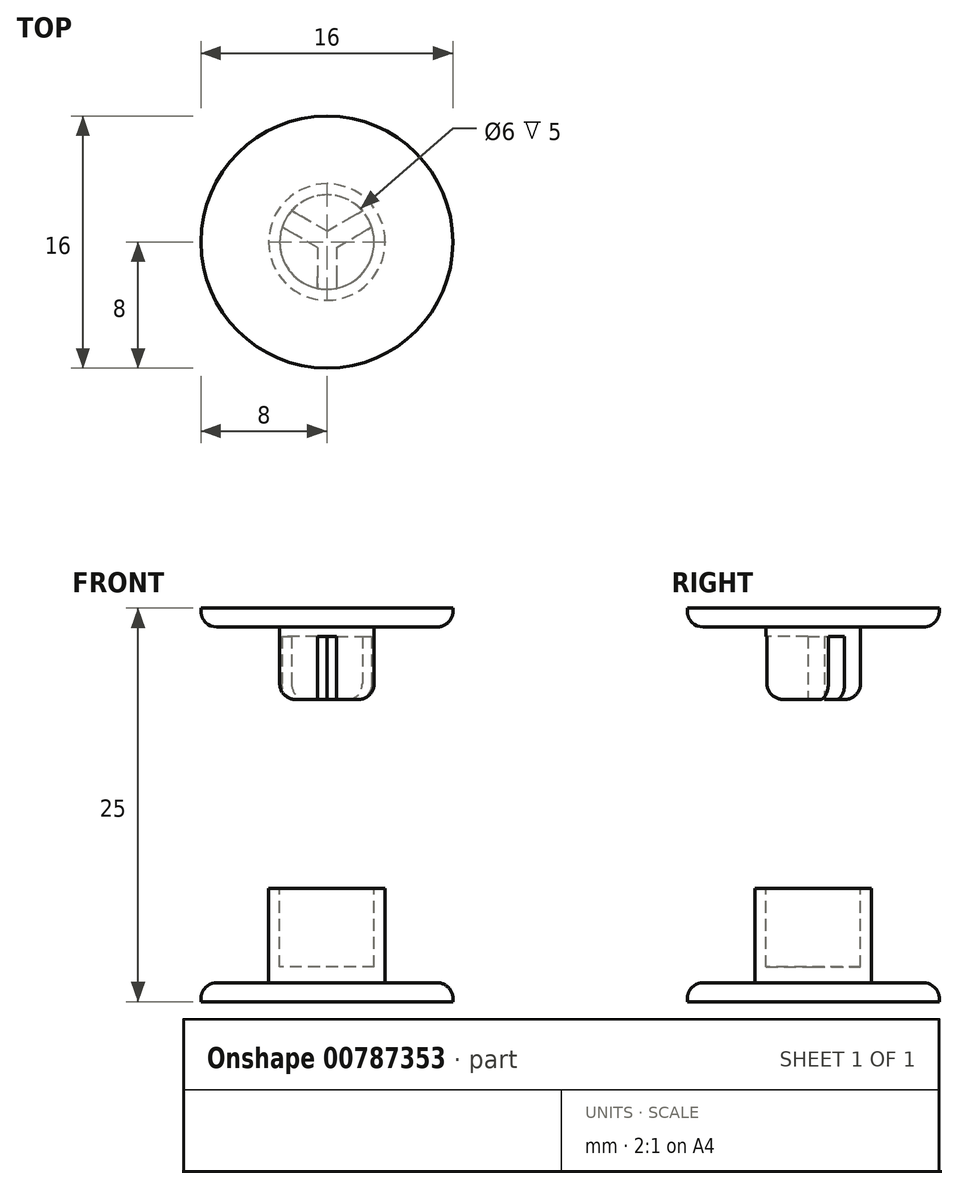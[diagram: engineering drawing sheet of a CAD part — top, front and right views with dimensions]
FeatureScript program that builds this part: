
annotation { "Feature Type Name" : "Feature", "Feature Type Description" : "" }
export const myFeature = defineFeature(function(context is Context, id is Id, definition is map)
    precondition{}
    {
        {
            var Q0;
            Q0=qCreatedBy(makeId("Top.planeOp"),FACE);
            var sketch = newSketch(context, id + "F0", { "sketchPlane" : qUnion([Q0])});
            skCircle(sketch, "E0", {"center": v(0, 0) * mm, "radius": 8 * mm});
            skSolve(sketch);
        }
        {
            var Q0;
            Q0 = qSketchRegion(id + "F0", true);
            extrude(context, id + "F1", {"entities" : qUnion([Q0]), "depth" : 1.2 * mm, "offsetDistance" : 25 * mm});
        }
        {
            var Q0;
            Q0=makeQuery(id+"F1.opExtrude","CAP_FACE",FACE,{"disambiguationData":[OSD([sQuery(id+"F0.wireOp",EDGE,"E0")])],"isStart":false});
            var sketch = newSketch(context, id + "F2", { "sketchPlane" : qUnion([Q0])});
            skCircle(sketch, "E1", {"center": v(0, 0) * mm, "radius": 3.7 * mm});
            skSolve(sketch);
        }
        {
            var Q0;
            Q0=makeQuery(id+"F2.imprint","IMPRINT",FACE,{"disambiguationData":[TD([[makeQuery(id+"F2.imprint","IMPRINT",EDGE,{"derivedFrom":sQuery(id+"F2.wireOp",EDGE,"E1")}),1.0]])]});
            extrude(context, id + "F3", {"entities" : qUnion([Q0]), "operationType" : NewBodyOperationType.ADD, "depth" : 6 * mm, "offsetDistance" : 25 * mm});
        }
        {
            var Q0;
            Q0=makeQuery(id+"F3.opExtrude","CAP_FACE",FACE,{"disambiguationData":[OSD([sQuery(id+"F2.wireOp",EDGE,"E1")])],"isStart":false});
            var sketch = newSketch(context, id + "F4", { "sketchPlane" : qUnion([Q0])});
            skCircle(sketch, "E2", {"center": v(0, 0) * mm, "radius": 3 * mm});
            skSolve(sketch);
        }
        {
            var Q0;
            Q0=makeQuery(id+"F4.imprint","IMPRINT",FACE,{"disambiguationData":[TD([[makeQuery(id+"F4.imprint","IMPRINT",EDGE,{"derivedFrom":sQuery(id+"F4.wireOp",EDGE,"E2")}),1.0]])]});
            extrude(context, id + "F5", {"entities" : qUnion([Q0]), "operationType" : NewBodyOperationType.REMOVE, "oppositeDirection" : true, "depth" : 5 * mm, "offsetDistance" : 25 * mm});
        }
        {
            var Q0;
            Q0=qCreatedBy(makeId("Top.planeOp"),FACE);
            cPlane(context, id + "F6", {"entities" : qUnion([Q0]), "cplaneType" : CPlaneType.OFFSET, "offset" : 25 * mm, "width" : 150 * mm, "height" : 150 * mm});
        }
        {
            var Q0;
            Q0=qCreatedBy(id+"F6.planeOp",FACE);
            var sketch = newSketch(context, id + "F7", { "sketchPlane" : qUnion([Q0])});
            skCircle(sketch, "E3", {"center": v(0, 0) * mm, "radius": 8 * mm});
            skSolve(sketch);
        }
        {
            var Q0;
            Q0 = qSketchRegion(id + "F7", true);
            extrude(context, id + "F8", {"entities" : qUnion([Q0]), "oppositeDirection" : true, "depth" : 1.2 * mm, "offsetDistance" : 25 * mm});
        }
        {
            var Q0;
            Q0=makeQuery(id+"F8.opExtrude","CAP_FACE",FACE,{"disambiguationData":[OSD([sQuery(id+"F7.wireOp",EDGE,"E3")])],"isStart":false});
            var sketch = newSketch(context, id + "F9", { "sketchPlane" : qUnion([Q0])});
            skCircle(sketch, "E4", {"center": v(0, 0) * mm, "radius": 3 * mm});
            skSolve(sketch);
        }
        {
            var Q0;
            Q0=makeQuery(id+"F9.imprint","IMPRINT",FACE,{"disambiguationData":[TD([[makeQuery(id+"F9.imprint","IMPRINT",EDGE,{"derivedFrom":sQuery(id+"F9.wireOp",EDGE,"E4")}),1.0]])]});
            extrude(context, id + "F10", {"entities" : qUnion([Q0]), "operationType" : NewBodyOperationType.ADD, "depth" : 4.6 * mm, "offsetDistance" : 25 * mm});
        }
        {
            var Q0;
            Q0=makeQuery(id+"F10.opExtrude","CAP_FACE",FACE,{"disambiguationData":[OSD([sQuery(id+"F9.wireOp",EDGE,"E4")])],"isStart":false});
            var sketch = newSketch(context, id + "F11", { "sketchPlane" : qUnion([Q0])});
            skCircle(sketch, "E5", {"center": v(0, 0) * mm, "radius": 0.6 * mm});
            skLineSegment(sketch, "E6", {"start": v(0, 0) * mm, "end": v(-6.93, -4) * mm, "construction": true});
            skLineSegment(sketch, "E7", {"start": v(6.93, -4) * mm, "end": v(0, 0) * mm, "construction": true});
            skLineSegment(sketch, "E8", {"start": v(0, 0) * mm, "end": v(0, 8) * mm, "construction": true});
            skLineSegment(sketch, "E9", {"start": v(0.6, 0.35) * mm, "end": v(0.6, 2.94) * mm});
            skLineSegment(sketch, "E10", {"start": v(0.6, 0.35) * mm, "end": v(2.85, -0.95) * mm});
            skLineSegment(sketch, "E11", {"start": v(-0.6, 0.35) * mm, "end": v(-0.6, 2.94) * mm});
            skLineSegment(sketch, "E12", {"start": v(-0.6, 0.35) * mm, "end": v(-2.85, -0.95) * mm});
            skLineSegment(sketch, "E13", {"start": v(0, -0.7) * mm, "end": v(-2.25, -1.99) * mm});
            skLineSegment(sketch, "E14.trimOffspring", {"start": v(0, -0.7) * mm, "end": v(2.25, -1.99) * mm});
            skPoint(sketch, "E15.orphan", {"position": v(-0.6, 0) * mm});
            skPoint(sketch, "E16.orphan", {"position": v(0.6, 0) * mm});
            skSolve(sketch);
        }
        {
            var Q0;
            Q0 = qSketchRegion(id + "F11", true);
            var Q1;
            {var subQ0=sQuery(id+"F11.wireOp",EDGE,"a1u6HoVm-Zr2R-fqAS-foof-CaSWl9cPsABc");Q1=makeQuery(id+"F11.imprint","IMPRINT",FACE,{"disambiguationData":[TD([[makeQuery(id+"F11.imprint","IMPRINT",EDGE,{"derivedFrom":subQ0}),-1.0]])]});}
            var Q2;
            {var subQ0=sQuery(id+"F11.wireOp",EDGE,"VQyUj8f5-NXvi-WfT6-4gmr-RtcVuqBwIcZW");Q2=makeQuery(id+"F11.imprint","IMPRINT",FACE,{"disambiguationData":[TD([[makeQuery(id+"F11.imprint","IMPRINT",EDGE,{"derivedFrom":subQ0}),1.0]])]});}
            var Q3;
            {var subQ2=sQuery(id+"F11.wireOp",EDGE,"hpf4cumQ-yglr-RZSq-RBKN-O2yOXngbCvaF");Q3=makeQuery(id+"F11.imprint","IMPRINT",FACE,{"disambiguationData":[TD([[makeQuery(id+"F11.imprint","IMPRINT",EDGE,{"derivedFrom":subQ2}),1.0]])]});}
            var Q4;
            {var subQ0=sQuery(id+"F11.wireOp",EDGE,"E12");var subQ1=sQuery(id+"F11.wireOp",EDGE,"3rWoFRl5-awWM-SBnq-aCvl-RjbUhyDCA5Gi");var subQ2=makeQuery(id+"F11.imprint","INTERSECT",VERTEX,{"derivedFrom":[subQ1,subQ0]});Q4=makeQuery(id+"F11.imprint","IMPRINT",FACE,{"disambiguationData":[TD([[makeQuery(id+"F11.imprint","IMPRINT",EDGE,{"disambiguationData":[TD([[subQ2,-1.0]])],"derivedFrom":subQ1}),-1.0]])]});}
            var Q5;
            {var subQ4=sQuery(id+"F11.wireOp",EDGE,"E10");var subQ5=makeQuery(id+"F10.opExtrude","CAP_EDGE",EDGE,{"disambiguationData":[OSD([sQuery(id+"F9.wireOp",EDGE,"E4")])],"isStart":false});var subQ6=makeQuery(id+"F11.imprint","INTERSECT",VERTEX,{"derivedFrom":[subQ5,subQ4]});Q5=makeQuery(id+"F11.imprint","IMPRINT",FACE,{"disambiguationData":[TD([[makeQuery(id+"F11.imprint","IMPRINT",EDGE,{"disambiguationData":[TD([[subQ6,1.0]])],"derivedFrom":subQ4}),-1.0]])]});}
            var Q6;
            {var subQ1=makeQuery(id+"F10.opExtrude","CAP_EDGE",EDGE,{"disambiguationData":[OSD([sQuery(id+"F9.wireOp",EDGE,"E4")])],"isStart":false});var subQ8=sQuery(id+"F11.wireOp",EDGE,"E9");var subQ11=makeQuery(id+"F11.imprint","INTERSECT",VERTEX,{"derivedFrom":[subQ1,subQ8]});Q6=makeQuery(id+"F11.imprint","IMPRINT",FACE,{"disambiguationData":[TD([[makeQuery(id+"F11.imprint","IMPRINT",EDGE,{"disambiguationData":[TD([[subQ11,1.0]])],"derivedFrom":subQ8}),1.0]])]});}
            extrude(context, id + "F12", {"entities" : qUnion([Q0, Q1, Q2, Q3, Q4, Q5, Q6]), "operationType" : NewBodyOperationType.REMOVE, "oppositeDirection" : true, "depth" : 4 * mm, "offsetDistance" : 25 * mm});
        }
        {
            var Q0;
            {var subQ0=sQuery(id+"F9.wireOp",EDGE,"E4");Q0=makeQuery(id+"F12.boolean.opBoolean","SPLIT",EDGE,{"disambiguationData":[TD([makeQuery(id+"F12.opExtrude","SWEPT_FACE",FACE,{"disambiguationData":[OSD([sQuery(id+"F11.wireOp",EDGE,"E11")])]})])],"derivedFrom":makeQuery(id+"F10.opExtrude","CAP_EDGE",EDGE,{"disambiguationData":[OSD([subQ0])],"isStart":false})});}
            var Q1;
            {var subQ0=sQuery(id+"F9.wireOp",EDGE,"E4");Q1=makeQuery(id+"F12.boolean.opBoolean","SPLIT",EDGE,{"disambiguationData":[TD([makeQuery(id+"F12.opExtrude","SWEPT_FACE",FACE,{"disambiguationData":[OSD([sQuery(id+"F11.wireOp",EDGE,"E9")])]})])],"derivedFrom":makeQuery(id+"F10.opExtrude","CAP_EDGE",EDGE,{"disambiguationData":[OSD([subQ0])],"isStart":false})});}
            var Q2;
            {var subQ0=sQuery(id+"F9.wireOp",EDGE,"E4");Q2=makeQuery(id+"F12.boolean.opBoolean","SPLIT",EDGE,{"disambiguationData":[TD([makeQuery(id+"F12.opExtrude","SWEPT_FACE",FACE,{"disambiguationData":[OSD([sQuery(id+"F11.wireOp",EDGE,"E13")])]})])],"derivedFrom":makeQuery(id+"F10.opExtrude","CAP_EDGE",EDGE,{"disambiguationData":[OSD([subQ0])],"isStart":false})});}
            var Q3;
            Q3=makeQuery(id+"F8.opExtrude","CAP_EDGE",EDGE,{"disambiguationData":[OSD([sQuery(id+"F7.wireOp",EDGE,"E3")])],"isStart":false});
            var Q4;
            Q4=makeQuery(id+"F5.boolean.opBoolean","COPY",EDGE,{"derivedFrom":makeQuery(id+"F5.opExtrude","CAP_EDGE",EDGE,{"disambiguationData":[OSD([sQuery(id+"F4.wireOp",EDGE,"E2")])],"isStart":true})});
            var Q5;
            Q5=makeQuery(id+"F1.opExtrude","CAP_EDGE",EDGE,{"disambiguationData":[OSD([sQuery(id+"F0.wireOp",EDGE,"E0")])],"isStart":false});
            fillet(context, id + "F13", {"entities" : qUnion([Q0, Q1, Q2, Q3, Q4, Q5]), "radius" : 1 * mm, "tangentPropagation" : true, "allowEdgeOverflow" : false});
        }
    });
